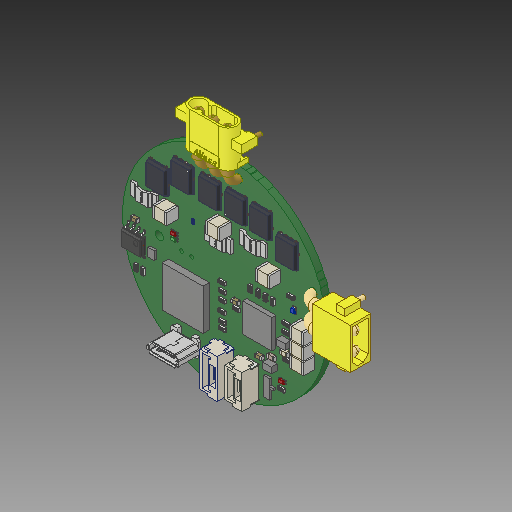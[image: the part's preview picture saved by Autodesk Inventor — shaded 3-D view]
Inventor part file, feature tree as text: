
AUTODESK INVENTOR PART (.ipt)
format: ipt  version: 2019.4 (Build 234330000, 330)  size: 7,354,368 bytes
history: native  units: mm
features: other x220, extrude x91, sketch x1, shell x1
ambient origin geometry x8: Origin, YZ Plane, XZ Plane, XY Plane, X Axis, Y Axis, Z Axis, Center Point
bodies: Solid1 (feature_tree), Solid2 (feature_tree), Solid3 (feature_tree), Solid4 (feature_tree), Solid5 (feature_tree), Solid6 (feature_tree), Solid7 (feature_tree), Solid8 (feature_tree), Solid9 (feature_tree), Solid10 (feature_tree), Solid11 (feature_tree), Solid12 (feature_tree), Solid13 (feature_tree), Solid14 (feature_tree), Solid15 (feature_tree), Solid16 (feature_tree), Solid17 (feature_tree), Solid18 (feature_tree), Solid19 (feature_tree), Solid20 (feature_tree), Solid21 (feature_tree), Solid22 (feature_tree), Solid23 (feature_tree), Solid24 (feature_tree), Solid25 (feature_tree), Solid26 (feature_tree), Solid27 (feature_tree), Solid28 (feature_tree), Solid29 (feature_tree), Solid30 (feature_tree), Solid31 (feature_tree), Solid32 (feature_tree), Solid33 (feature_tree), Solid34 (feature_tree), Solid35 (feature_tree), Solid36 (feature_tree), Solid37 (feature_tree), Solid38 (feature_tree), Solid39 (feature_tree), Solid40 (feature_tree), Solid41 (feature_tree), Solid42 (feature_tree), Solid43 (feature_tree), Solid44 (feature_tree), Solid45 (feature_tree), Solid46 (feature_tree), Solid47 (feature_tree), Solid48 (feature_tree), Solid49 (feature_tree), Solid50 (feature_tree), Solid51 (feature_tree), Solid52 (feature_tree), Solid53 (feature_tree), Solid54 (feature_tree), Solid55 (feature_tree), Solid56 (feature_tree), Solid57 (feature_tree), Solid58 (feature_tree), Solid59 (feature_tree), Solid60 (feature_tree), Solid61 (feature_tree), Solid62 (feature_tree), Solid63 (feature_tree), Solid64 (feature_tree), Solid65 (feature_tree), Solid66 (feature_tree), Solid67 (feature_tree), Solid68 (feature_tree), Solid69 (feature_tree), Solid70 (feature_tree), Solid71 (feature_tree), Solid72 (feature_tree), Solid73 (feature_tree), Solid74 (feature_tree), Solid75 (feature_tree), Solid76 (feature_tree), Solid77 (feature_tree), Solid78 (feature_tree), Solid79 (feature_tree), Solid80 (feature_tree), Solid81 (feature_tree), Solid82 (feature_tree), Solid83 (feature_tree), Solid84 (feature_tree), Solid85 (feature_tree), Solid86 (feature_tree), Solid87 (feature_tree), Solid88 (feature_tree), Solid89 (feature_tree), Solid90 (feature_tree), Solid91 (feature_tree), Solid92 (feature_tree), Solid93 (feature_tree), Solid94 (feature_tree), Solid95 (feature_tree), Solid96 (feature_tree), Solid97 (feature_tree), Solid98 (feature_tree), Solid99 (feature_tree), Solid100 (feature_tree), Solid101 (feature_tree), Solid102 (feature_tree), Solid103 (feature_tree), Solid104 (feature_tree), Solid105 (feature_tree), Solid106 (feature_tree), Solid107 (feature_tree), Solid108 (feature_tree), Solid109 (feature_tree), Solid110 (feature_tree), Solid111 (feature_tree), Solid112 (feature_tree), Solid113 (feature_tree), Solid114 (feature_tree), Solid115 (feature_tree), Solid116 (feature_tree), Solid117 (feature_tree), Solid118 (feature_tree), Solid119 (feature_tree), Solid120 (feature_tree), Solid121 (feature_tree), Solid122 (feature_tree), Solid123 (feature_tree), Solid124 (feature_tree), Solid125 (feature_tree), Solid126 (feature_tree), Solid127 (feature_tree), Solid128 (feature_tree), Solid129 (feature_tree), Solid130 (feature_tree), Solid131 (feature_tree), Solid132 (feature_tree), Solid133 (feature_tree), Solid134 (feature_tree), Solid135 (feature_tree), Solid136 (feature_tree), Solid137 (feature_tree), Solid138 (feature_tree), Solid139 (feature_tree), Solid140 (feature_tree), Solid141 (feature_tree), Solid142 (feature_tree), Solid143 (feature_tree), Solid144 (feature_tree), Solid145 (feature_tree), Solid146 (feature_tree), Solid147 (feature_tree), Solid148 (feature_tree), Solid149 (feature_tree), Solid150 (feature_tree), Solid151 (feature_tree), Solid152 (feature_tree), Solid153 (feature_tree), Solid154 (feature_tree), Solid155 (feature_tree), Solid156 (feature_tree), Solid157 (feature_tree), Solid158 (feature_tree), Solid159 (feature_tree), Solid160 (feature_tree), Solid161 (feature_tree), Solid162 (feature_tree), Solid163 (feature_tree), Solid164 (feature_tree), Solid165 (feature_tree), Solid166 (feature_tree), Solid167 (feature_tree), Solid168 (feature_tree), Solid169 (feature_tree), Solid170 (feature_tree), Solid171 (feature_tree), Solid172 (feature_tree), Solid173 (feature_tree), Solid174 (feature_tree), Solid175 (feature_tree), Solid176 (feature_tree), Solid177 (feature_tree), Solid178 (feature_tree), Solid179 (feature_tree), Solid180 (feature_tree), Solid181 (feature_tree), Solid182 (feature_tree), Solid183 (feature_tree), Solid184 (feature_tree), Solid185 (feature_tree), Solid186 (feature_tree), Solid187 (feature_tree), Solid188 (feature_tree), Solid189 (feature_tree), Solid190 (feature_tree), Solid191 (feature_tree), Solid192 (feature_tree), Solid193 (feature_tree), Solid194 (feature_tree), Solid195 (feature_tree), Solid196 (feature_tree), Solid197 (feature_tree), Solid198 (feature_tree), Solid199 (feature_tree), Solid200 (feature_tree), Solid201 (feature_tree), Solid202 (feature_tree), Solid203 (feature_tree), Solid204 (feature_tree), Solid205 (feature_tree), Solid206 (feature_tree), Solid207 (feature_tree), Solid208 (feature_tree), Solid209 (feature_tree), Solid210 (feature_tree), Solid211 (feature_tree), Solid212 (feature_tree), Solid213 (feature_tree), Solid214 (feature_tree), Solid215 (feature_tree), Solid216 (feature_tree), Solid217 (feature_tree), Solid218 (feature_tree), Solid219 (feature_tree), Solid220 (feature_tree), Solid221 (feature_tree), Solid222 (feature_tree), Solid223 (feature_tree), Solid224 (feature_tree), Solid225 (feature_tree), Solid226 (feature_tree), Solid227 (feature_tree), Solid228 (feature_tree), Solid229 (feature_tree), Solid230 (feature_tree), Solid231 (feature_tree), Solid232 (feature_tree), Solid233 (feature_tree), Solid234 (feature_tree), Solid235 (feature_tree), Solid236 (feature_tree), Solid237 (feature_tree), Solid238 (feature_tree), Solid239 (feature_tree), Solid240 (feature_tree), Solid241 (feature_tree), Solid242 (feature_tree), Solid243 (feature_tree), Solid244 (feature_tree), Solid245 (feature_tree), Solid246 (feature_tree), Solid247 (feature_tree), Solid248 (feature_tree), Solid249 (feature_tree), Solid250 (feature_tree), Solid251 (feature_tree), Solid252 (feature_tree), Solid253 (feature_tree), Solid254 (feature_tree), Solid255 (feature_tree), Solid256 (feature_tree), Solid257 (feature_tree), Solid258 (feature_tree), Solid259 (feature_tree), Solid260 (feature_tree), Solid261 (feature_tree), Solid262 (feature_tree), Solid263 (feature_tree), Solid264 (feature_tree), Solid265 (feature_tree), Solid266 (feature_tree), Solid267 (feature_tree), Solid268 (feature_tree), Solid269 (feature_tree), Solid270 (feature_tree), Solid271 (feature_tree), Solid272 (feature_tree), Solid273 (feature_tree), Solid274 (feature_tree), Solid275 (feature_tree), Solid276 (feature_tree), Solid277 (feature_tree), Solid278 (feature_tree), Solid279 (feature_tree), Solid280 (feature_tree), Solid281 (feature_tree), Solid282 (feature_tree), Solid283 (feature_tree), Solid284 (feature_tree), Solid285 (feature_tree), Solid286 (feature_tree), Solid287 (feature_tree), Solid288 (feature_tree), Solid289 (feature_tree), Solid290 (feature_tree), Solid291 (feature_tree), Solid292 (feature_tree), Solid293 (feature_tree), Solid294 (feature_tree), Solid295 (feature_tree), Solid296 (feature_tree), Solid297 (feature_tree), Solid298 (feature_tree), Solid299 (feature_tree), Solid300 (feature_tree), Solid301 (feature_tree), Solid302 (feature_tree), Solid303 (feature_tree), Solid304 (feature_tree), Solid305 (feature_tree), Solid306 (feature_tree), Solid307 (feature_tree), Solid308 (feature_tree), Solid309 (feature_tree)
feature tree (313):
  extrude  "Extrusion1"  Depth=30.0mm TaperAngle=0.0deg
  sketch  "Sketch1"  dims[d0=50.0mm d1=30.0mm d2=30.0mm d3=0.0mm d4=0.0mm d5=16.000001mm]
  other  "Board_1:1"
  extrude  "Extruded_2:1"  Depth=16.000001mm
  extrude  "Extruded_2:2"  [1 undecoded]
  other  "JST_BM04B-GHS-TBT_7:1"
  other  "0603_resistor_9:1"
  other  "0603_resistor_9:2"
  other  "TER2-2_11:1"
  other  "TER2-1_12:1"
  other  "TER2_13:1"
  other  "TER2-3_14:1"
  other  "TER2-4_15:1"
  other  "HOUSING-1_17:1"
  shell  "SHELL_18:1"  [1 undecoded]
  extrude  "Extruded_21:1"  [1 undecoded]
  extrude  "Extruded_24:1"  [1 undecoded]
  extrude  "Extruded_27:1"  [1 undecoded]
  extrude  "Extruded_29:1"  [1 undecoded]
  extrude  "Extruded_29:2"  [1 undecoded]
  other  "0603_cap_33:1"
  extrude  "Extruded_35:1"  [1 undecoded]
  extrude  "Extruded_37:1"  [1 undecoded]
  extrude  "Extruded_35:2"  [1 undecoded]
  other  "User_Library-DFN5x6_SO8FL_Extruded_41:1"
  other  "User_Library-DFN5x6_SO8FL_Extruded_2_43:1"
  other  "User_Library-DFN5x6_SO8FL_Extruded_2_43:2"
  other  "User_Library-DFN5x6_SO8FL_Extruded_41:2"
  other  "User_Library-DFN5x6_SO8FL_Cylinder_47:1"
  other  "User_Library-DFN5x6_SO8FL_Extruded_3_49:1"
  other  "User_Library-DFN5x6_SO8FL_Extruded_4_51:1"
  other  "User_Library-DFN5x6_SO8FL_Extruded_5_53:1"
  other  "User_Library-DFN5x6_SO8FL_Extruded_5_53:2"
  other  "User_Library-DFN5x6_SO8FL_Extruded_5_53:3"
  other  "User_Library-DFN5x6_SO8FL_Extruded_5_53:4"
  other  "User_Library-DFN5x6_SO8FL_Extruded_6_58:1"
  extrude  "Extruded_63:1"  [1 undecoded]
  other  "0603_resistor_66:1"
  other  "0603_resistor_66:2"
  other  "0603_resistor_68:1"
  other  "0603_resistor_68:2"
  other  "0603_resistor_70:1"
  other  "0603_resistor_70:2"
  other  "0603_resistor_72:1"
  other  "0603_resistor_72:2"
  extrude  "Extruded_74:1"  [1 undecoded]
  extrude  "Extruded_76:1"  [1 undecoded]
  extrude  "Extruded_76:2"  [1 undecoded]
  extrude  "Extruded_80:1"  [1 undecoded]
  extrude  "Extruded_82:1"  [1 undecoded]
  extrude  "Extruded_82:2"  [1 undecoded]
  extrude  "Extruded_82:3"  [1 undecoded]
  extrude  "Extruded_82:4"  [1 undecoded]
  extrude  "Extruded_80:2"  [1 undecoded]
  other  "0603_cap_90:1"
  other  "0603_cap_92:1"
  other  "0603_cap_94:1"
  extrude  "Extruded_82:5"  [1 undecoded]
  extrude  "Extruded_82:6"  [1 undecoded]
  extrude  "Extruded_80:3"  [1 undecoded]
  extrude  "Extruded_100:1"  [1 undecoded]
  extrude  "Extruded_100:2"  [1 undecoded]
  extrude  "Extruded_103:1"  [1 undecoded]
  extrude  "Extruded_100:3"  [1 undecoded]
  extrude  "Extruded_100:4"  [1 undecoded]
  extrude  "Extruded_103:2"  [1 undecoded]
  extrude  "Extruded_100:5"  [1 undecoded]
  extrude  "Extruded_100:6"  [1 undecoded]
  extrude  "Extruded_103:3"  [1 undecoded]
  extrude  "Extruded_80:4"  [1 undecoded]
  extrude  "Extruded_82:7"  [1 undecoded]
  extrude  "Extruded_82:8"  [1 undecoded]
  extrude  "Extruded_80:5"  [1 undecoded]
  extrude  "Extruded_82:9"  [1 undecoded]
  extrude  "Extruded_82:10"  [1 undecoded]
  extrude  "Extruded_80:6"  [1 undecoded]
  extrude  "Extruded_82:11"  [1 undecoded]
  extrude  "Extruded_82:12"  [1 undecoded]
  extrude  "Extruded_80:7"  [1 undecoded]
  extrude  "Extruded_82:13"  [1 undecoded]
  extrude  "Extruded_82:14"  [1 undecoded]
  extrude  "Extruded_80:8"  [1 undecoded]
  extrude  "Extruded_82:15"  [1 undecoded]
  extrude  "Extruded_82:16"  [1 undecoded]
  extrude  "Extruded_80:9"  [1 undecoded]
  extrude  "Extruded_82:17"  [1 undecoded]
  extrude  "Extruded_82:18"  [1 undecoded]
  extrude  "Extruded_138:1"  [1 undecoded]
  extrude  "Extruded_140:1"  [1 undecoded]
  extrude  "Extruded_140:2"  [1 undecoded]
  other  "User_Library-MR30PW-M_144:1"
  extrude  "Extruded_146:1"  [1 undecoded]
  extrude  "Extruded_149:1"  [1 undecoded]
  extrude  "Extruded_152:1"  [1 undecoded]
  other  "User_Library-SOT-223-2_PIN_SOT-223_2_1_155:1"
  other  "User_Library-SOT-223-2_SOT-223_1_156:1"
  other  "User_Library-SOT-223-2_PIN_SOT-223_2_1_157:1"
  other  "User_Library-SOT-223-2_PIN_SOT-223_1_158:1"
  other  "User_Library-SOT-223-2_PIN_SOT-223_2_1_159:1"
  other  "0603_resistor_162:1"
  other  "0603_resistor_162:2"
  other  "0603_resistor_164:1"
  other  "0603_resistor_164:2"
  other  "0603_resistor_166:1"
  other  "0603_resistor_166:2"
  other  "0603_resistor_168:1"
  other  "0603_resistor_168:2"
  other  "0603_resistor_170:1"
  other  "0603_resistor_170:2"
  other  "0603_resistor_172:1"
  other  "0603_resistor_172:2"
  other  "0603_resistor_174:1"
  other  "0603_resistor_174:2"
  other  "0603_resistor_176:1"
  other  "0603_resistor_176:2"
  other  "0603_resistor_178:1"
  other  "0603_resistor_178:2"
  other  "0603_resistor_180:1"
  other  "0603_resistor_180:2"
  extrude  "Extruded_35:3"  [1 undecoded]
  extrude  "Extruded_37:2"  [1 undecoded]
  extrude  "Extruded_35:4"  [1 undecoded]
  other  "0603_resistor_186:1"
  other  "0603_resistor_186:2"
  other  "CSS2H-2512K-2L00F_188:1"
  other  "0603_resistor_190:1"
  other  "0603_resistor_190:2"
  other  "0603_resistor_192:1"
  other  "0603_resistor_192:2"
  other  "0603_resistor_194:1"
  other  "0603_resistor_194:2"
  other  "0603_resistor_196:1"
  other  "0603_resistor_196:2"
  other  "CSS2H-2512K-2L00F_198:1"
  other  "0603_resistor_200:1"
  other  "0603_resistor_200:2"
  other  "0603_resistor_202:1"
  other  "0603_resistor_202:2"
  other  "0603_resistor_204:1"
  other  "0603_resistor_204:2"
  other  "0603_resistor_206:1"
  other  "0603_resistor_206:2"
  other  "0603_resistor_208:1"
  other  "0603_resistor_208:2"
  other  "CSS2H-2512K-2L00F_210:1"
  other  "0402_resistor_212:1"
  other  "0402_resistor_212:2"
  other  "0603_resistor_214:1"
  other  "0603_resistor_214:2"
  other  "0603_resistor_216:1"
  other  "0603_resistor_216:2"
  other  "0603_resistor_218:1"
  other  "0603_resistor_218:2"
  other  "0603_resistor_220:1"
  other  "0603_resistor_220:2"
  other  "0603_resistor_222:1"
  other  "0603_resistor_222:2"
  other  "0603_resistor_224:1"
  other  "0603_resistor_224:2"
  other  "0603_resistor_226:1"
  other  "0603_resistor_226:2"
  other  "0603_resistor_228:1"
  other  "0603_resistor_228:2"
  other  "0603_resistor_230:1"
  other  "0603_resistor_230:2"
  other  "0603_resistor_232:1"
  other  "0603_resistor_232:2"
  other  "User_Library-DFN5x6_SO8FL_Extruded_41:3"
  other  "User_Library-DFN5x6_SO8FL_Extruded_2_43:3"
  other  "User_Library-DFN5x6_SO8FL_Extruded_2_43:4"
  other  "User_Library-DFN5x6_SO8FL_Extruded_41:4"
  other  "User_Library-DFN5x6_SO8FL_Cylinder_47:2"
  other  "User_Library-DFN5x6_SO8FL_Extruded_3_49:2"
  other  "User_Library-DFN5x6_SO8FL_Extruded_4_51:2"
  other  "User_Library-DFN5x6_SO8FL_Extruded_5_53:5"
  other  "User_Library-DFN5x6_SO8FL_Extruded_5_53:6"
  other  "User_Library-DFN5x6_SO8FL_Extruded_5_53:7"
  other  "User_Library-DFN5x6_SO8FL_Extruded_5_53:8"
  other  "User_Library-DFN5x6_SO8FL_Extruded_6_58:2"
  other  "User_Library-DFN5x6_SO8FL_Extruded_41:5"
  other  "User_Library-DFN5x6_SO8FL_Extruded_2_43:5"
  other  "User_Library-DFN5x6_SO8FL_Extruded_2_43:6"
  other  "User_Library-DFN5x6_SO8FL_Extruded_41:6"
  other  "User_Library-DFN5x6_SO8FL_Cylinder_47:3"
  other  "User_Library-DFN5x6_SO8FL_Extruded_3_49:3"
  other  "User_Library-DFN5x6_SO8FL_Extruded_4_51:3"
  other  "User_Library-DFN5x6_SO8FL_Extruded_5_53:9"
  other  "User_Library-DFN5x6_SO8FL_Extruded_5_53:10"
  other  "User_Library-DFN5x6_SO8FL_Extruded_5_53:11"
  other  "User_Library-DFN5x6_SO8FL_Extruded_5_53:12"
  other  "User_Library-DFN5x6_SO8FL_Extruded_6_58:3"
  other  "body_30xx_238:1"
  other  "land_pattern_30xx_239:1"
  other  "land_pattern_30xx_240:1"
  other  "FER_0603_243:1"
  other  "JST_BM05B-GHS-TBT_245:1"
  other  "LED_0603_Base_RED_247:1"
  other  "LED_0603_Base_RED_247:2"
  other  "LED_0603_Lens_RED_248:1"
  extrude  "Extruded_250:1"  [1 undecoded]
  other  "LED_0603_Lens_BLUE_255:1"
  other  "LED_0603_Base_BLUE_256:1"
  other  "LED_0603_Base_BLUE_256:2"
  other  "LED_0603_Lens_GREEN_258:1"
  other  "LED_0603_Base_GREEN_259:1"
  other  "LED_0603_Base_GREEN_259:2"
  other  "LED_0603_Base_RED_261:1"
  other  "LED_0603_Base_RED_261:2"
  other  "LED_0603_Lens_RED_262:1"
  other  "0402_cap_264:1"
  other  "0603_cap_266:1"
  other  "0603_cap_268:1"
  other  "0402_cap_270:1"
  other  "0603_cap_272:1"
  extrude  "Extruded_82:19"  [1 undecoded]
  extrude  "Extruded_82:20"  [1 undecoded]
  extrude  "Extruded_80:10"  [1 undecoded]
  extrude  "Extruded_29:3"  [1 undecoded]
  extrude  "Extruded_29:4"  [1 undecoded]
  extrude  "Extruded_27:2"  [1 undecoded]
  extrude  "Extruded_82:21"  [1 undecoded]
  extrude  "Extruded_82:22"  [1 undecoded]
  extrude  "Extruded_80:11"  [1 undecoded]
  other  "0603_cap_286:1"
  extrude  "Extruded_63:2"  [1 undecoded]
  other  "0603_cap_290:1"
  other  "0603_cap_292:1"
  extrude  "Extruded_294:1"  [1 undecoded]
  extrude  "Extruded_294:2"  [1 undecoded]
  extrude  "Extruded_297:1"  [1 undecoded]
  other  "0603_cap_300:1"
  extrude  "Extruded_294:3"  [1 undecoded]
  extrude  "Extruded_294:4"  [1 undecoded]
  extrude  "Extruded_297:2"  [1 undecoded]
  other  "0603_cap_306:1"
  extrude  "Extruded_29:5"  [1 undecoded]
  extrude  "Extruded_29:6"  [1 undecoded]
  extrude  "Extruded_27:3"  [1 undecoded]
  other  "0603_cap_312:1"
  other  "0603_cap_314:1"
  other  "0603_cap_316:1"
  other  "0603_cap_318:1"
  other  "0603_cap_320:1"
  other  "0603_cap_322:1"
  other  "0603_cap_324:1"
  other  "0603_cap_326:1"
  other  "0603_cap_328:1"
  other  "0603_cap_330:1"
  other  "User_Library-XT30-_curved_332:1"
  other  "User_Library-XT30-_curved_332:2"
  other  "User_Library-XT30-_curved_332:3"
  extrude  "Extruded_80:12"  [1 undecoded]
  extrude  "Extruded_82:23"  [1 undecoded]
  extrude  "Extruded_82:24"  [1 undecoded]
  extrude  "Extruded_100:7"  [1 undecoded]
  extrude  "Extruded_100:8"  [1 undecoded]
  extrude  "Extruded_103:4"  [1 undecoded]
  extrude  "Extruded_342:1"  [1 undecoded]
  other  "BODY_M08A_35_345:1"
  other  "LEAD_M08A_57_346:1"
  other  "LEAD_M08A_57_347:1"
  other  "LEAD_M08A_57_348:1"
  other  "LEAD_M08A_57_349:1"
  other  "LEAD_M08A_57_350:1"
  other  "LEAD_M08A_57_351:1"
  other  "LEAD_M08A_57_352:1"
  other  "LEAD_M08A_57_353:1"
  other  "MANIFOLD_SOLID_BREP_2784_354:1"
  other  "MANIFOLD_SOLID_BREP_2935_355:1"
  other  "MANIFOLD_SOLID_BREP_3086_356:1"
  other  "MANIFOLD_SOLID_BREP_3237_357:1"
  extrude  "Extruded_362:1"  [1 undecoded]
  extrude  "Extruded_365:1"  [1 undecoded]
  extrude  "Extruded_368:1"  [1 undecoded]
  extrude  "Extruded_370:1"  [1 undecoded]
  other  "User_Library-DFN5x6_SO8FL_Extruded_41:7"
  other  "User_Library-DFN5x6_SO8FL_Extruded_2_43:7"
  other  "User_Library-DFN5x6_SO8FL_Extruded_2_43:8"
  other  "User_Library-DFN5x6_SO8FL_Extruded_41:8"
  other  "User_Library-DFN5x6_SO8FL_Cylinder_47:4"
  other  "User_Library-DFN5x6_SO8FL_Extruded_3_49:4"
  other  "User_Library-DFN5x6_SO8FL_Extruded_4_51:4"
  other  "User_Library-DFN5x6_SO8FL_Extruded_5_53:13"
  other  "User_Library-DFN5x6_SO8FL_Extruded_5_53:14"
  other  "User_Library-DFN5x6_SO8FL_Extruded_5_53:15"
  other  "User_Library-DFN5x6_SO8FL_Extruded_5_53:16"
  other  "User_Library-DFN5x6_SO8FL_Extruded_6_58:4"
  other  "User_Library-DFN5x6_SO8FL_Extruded_41:9"
  other  "User_Library-DFN5x6_SO8FL_Extruded_2_43:9"
  other  "User_Library-DFN5x6_SO8FL_Extruded_2_43:10"
  other  "User_Library-DFN5x6_SO8FL_Extruded_41:10"
  other  "User_Library-DFN5x6_SO8FL_Cylinder_47:5"
  other  "User_Library-DFN5x6_SO8FL_Extruded_3_49:5"
  other  "User_Library-DFN5x6_SO8FL_Extruded_4_51:5"
  other  "User_Library-DFN5x6_SO8FL_Extruded_5_53:17"
  other  "User_Library-DFN5x6_SO8FL_Extruded_5_53:18"
  other  "User_Library-DFN5x6_SO8FL_Extruded_5_53:19"
  other  "User_Library-DFN5x6_SO8FL_Extruded_5_53:20"
  other  "User_Library-DFN5x6_SO8FL_Extruded_6_58:5"
  other  "User_Library-DFN5x6_SO8FL_Extruded_41:11"
  other  "User_Library-DFN5x6_SO8FL_Extruded_2_43:11"
  other  "User_Library-DFN5x6_SO8FL_Extruded_2_43:12"
  other  "User_Library-DFN5x6_SO8FL_Extruded_41:12"
  other  "User_Library-DFN5x6_SO8FL_Cylinder_47:6"
  other  "User_Library-DFN5x6_SO8FL_Extruded_3_49:6"
  other  "User_Library-DFN5x6_SO8FL_Extruded_4_51:6"
  other  "User_Library-DFN5x6_SO8FL_Extruded_5_53:21"
  other  "User_Library-DFN5x6_SO8FL_Extruded_5_53:22"
  other  "User_Library-DFN5x6_SO8FL_Extruded_5_53:23"
  other  "User_Library-DFN5x6_SO8FL_Extruded_5_53:24"
  other  "User_Library-DFN5x6_SO8FL_Extruded_6_58:6"
  other  "Composite1"
  other  "Srf1"
note: 90 required parameter values undecoded (feature->parameter linkage not recoverable at this tier; creation-order binding heuristic only, values carry confidence <= 0.55)
